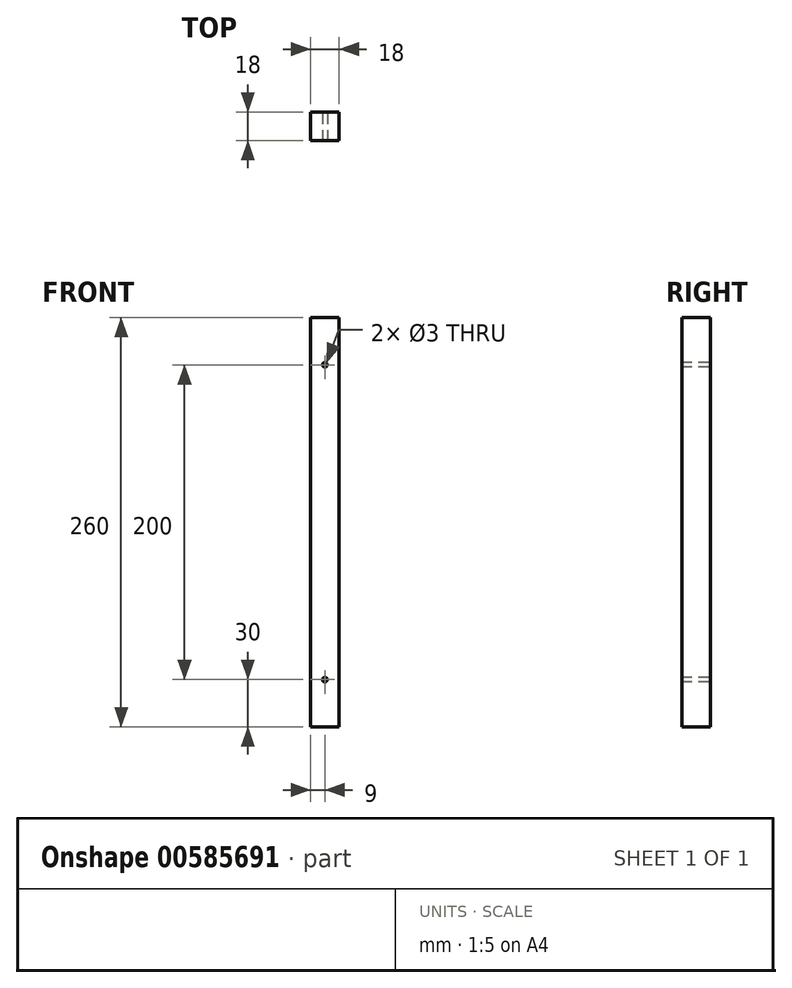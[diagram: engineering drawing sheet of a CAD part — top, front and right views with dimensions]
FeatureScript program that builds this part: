
annotation { "Feature Type Name" : "Feature", "Feature Type Description" : "" }
export const myFeature = defineFeature(function(context is Context, id is Id, definition is map)
    precondition{}
    {
        {
            var Q0;
            Q0=qCreatedBy(makeId("Top.planeOp"),FACE);
            var sketch = newSketch(context, id + "F0", { "sketchPlane" : qUnion([Q0])});
            skLineSegment(sketch, "E0.bottom", {"start": v(0, 0) * mm, "end": v(-18, 0) * mm});
            skLineSegment(sketch, "E0.top", {"start": v(0, -18) * mm, "end": v(-18, -18) * mm});
            skLineSegment(sketch, "E0.left", {"start": v(0, 0) * mm, "end": v(0, -18) * mm});
            skLineSegment(sketch, "E0.right", {"start": v(-18, 0) * mm, "end": v(-18, -18) * mm});
            skSolve(sketch);
        }
        {
            var Q0;
            Q0=makeQuery(id+"F0.imprint","IMPRINT",FACE,{"disambiguationData":[TD([[makeQuery(id+"F0.imprint","IMPRINT",EDGE,{"derivedFrom":sQuery(id+"F0.wireOp",EDGE,"E0.bottom")}),1.0]])]});
            extrude(context, id + "F1", {"entities" : qUnion([Q0]), "depth" : 260 * mm, "offsetDistance" : 25 * mm});
        }
        {
            var Q0;
            Q0=makeQuery(id+"F1.opExtrude","SWEPT_FACE",FACE,{"disambiguationData":[OSD([sQuery(id+"F0.wireOp",EDGE,"E0.top")])]});
            var sketch = newSketch(context, id + "F2", { "sketchPlane" : qUnion([Q0])});
            skCircle(sketch, "E1", {"center": v(-9, 230) * mm, "radius": 1.5 * mm});
            skCircle(sketch, "E2", {"center": v(-9, 30) * mm, "radius": 1.5 * mm});
            skSolve(sketch);
        }
        {
            var Q0;
            Q0 = qSketchRegion(id + "F2", true);
            extrude(context, id + "F3", {"entities" : qUnion([Q0]), "operationType" : NewBodyOperationType.REMOVE, "endBound" : BoundingType.THROUGH_ALL, "oppositeDirection" : true, "depth" : 25 * mm, "offsetDistance" : 25 * mm});
        }
    });
